# Revit family: Furniture_Office-Chairs_Flokk_Giroflex-64
name_source: partatom
category: Furniture
units: mm (PartAtom-declared; Revit-internal decimal feet)

## family parameters
Always vertical = Yes
Cut with Voids When Loaded = No
OmniClass Number = 23.40.20.14.14.11
OmniClass Title = Chairs
Room Calculation Point = No
Shared = No
Work Plane-Based = No

## types (1)
- Giroflex 64
    AssetType = Movable
    BIMObjectName = Furniture_Office-Chairs_Flokk_Giroflex-64
    Brand = Flokk
    Category = Giroflex
    Color = Various
    Cost = 0 $
    Default Elevation = 0 mm  [stored 0 ft]
    Description = The giroflex 64 swivel chair stands for noticeably correct sitting. This globally loved classic guarantees perfect seating comfort.
    Designer = Walser Design / Paolo Fancelli
    DurationUnit = Year
    IfcExportAs = IfcFurnishingElementType
    IfcExportType = CHAIR
    LowestSeatingHeight = 500 mm  [stored 1.64042 ft]
    MainColor = Various
    Manufacturer = Flokk
    ManufacturerName = Flokk
    ManufacturerURL = https://www.flokk.com
    Material = Plastic, Metal and Textile
    Model = Giroflex 64
    ModelNumber = 64-3578
    NBSDescription = Stacking chairs
    NBSReference = 45-35-20/355
    Name = Giroflex-64
    NominalDepth = 570 mm
    NominalLength = 514 mm
    OfficeChairQuaternaryMaterial = Black RAL 9005
    ProductDatasheet = https://flokkplatformprod.blob.core.windows.net
    ProductInformation = Swivel chair The giroflex 64 swivel chair stands for noticeably correct sitting. This global million seller classic of office furnishings, guarantees perfect seating comfort. The technical perfections and the scientifically tested ergonomics allow the giroflex 64 swivel chairs offer its users optimal support in every sitting position.

The individuality of the occupants is reflected in the variety of seat and back sizes. This Swivel chair has Standard seat width 45 cm Medium back height 55-62 cm

The dual-zone seat profile used on this chair for the first time ensures support and wellbeing.
    SeatingHeight = 500 mm  [stored 1.64042 ft]
    Shape = Sculptured
    Size = 515x570x1060 mm
    URL = https://store.flokk.com
    Uniclass2 = Pr_40_50_12_51
    Uniclass2015Description = Meeting room chairs
    Uniclass2015Reference = Pr_40_50_12_51
    Version = 1
    VersionDate = 10/01/2022
    WarrantyDurationUnit = Year

note: [stored X ft] marks values corroborated as IEEE doubles in the binary element streams (Revit-internal decimal feet)

## geometry (parser evidence)
native form markers: Sweep x6
no freeform markers — native parametric forms only
